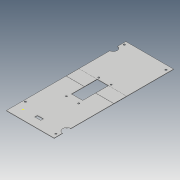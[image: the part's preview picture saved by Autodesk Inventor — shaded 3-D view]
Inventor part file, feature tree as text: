
AUTODESK INVENTOR PART (.ipt)
format: ipt  version: 2019 (Build 230136000, 136)  size: 241,152 bytes
history: native  units: mm
features: move_body x8, sketch x7, reference x6, extrude x5, other x5, direct_edit x3, plane x1, fillet x1, split x1
ambient origin geometry x8: Origin, YZ Plane, XZ Plane, XY Plane, X Axis, Y Axis, Z Axis, Center Point
bodies: Solid1 (feature_tree), Solid2 (feature_tree), Solid3 (feature_tree)
feature tree (37):
  plane  "Work Plane1"
  extrude  "Extrusion1"  Depth=2.0mm TaperAngle=0.0deg
  extrude  "Extrusion2"  Depth=29.0mm
  sketch  "Sketch3"  dims[d6=4.0mm d7=4.0mm d8=4.0mm]
  extrude  "Extrusion4"  Depth=4.0mm
  fillet  "Fillet1"  Radius=4.0mm
  extrude  "Extrusion5"  Depth=5.5mm
  split  "Split1"
  sketch  "Sketch7"  dims[d14=11.8mm d15=1.4mm d16=1.4mm d17=11.8mm d20=20.0mm d21=2.0mm d22=0.0mm d23=1.0mm d24=280.0mm d25=7.0mm d26=15.5mm d27=10.0mm d28=0.0mm d29=10.0mm d30=0.0mm d34=0.0mm d35=0.0mm d36=-1.0mm d37=0.0mm d38=0.0mm d39=-1.0mm d40=0.0mm d41=0.0mm d42=-1.0mm d43=0.0mm d44=0.0mm d45=-1.0mm d46=0.0mm d47=0.0mm d48=-1.0mm d49=0.0mm d50=0.0mm d51=-1.0mm d52=20.0mm d53=0.0mm d54=0.0mm d55=-1.0mm d56=0.0mm d57=0.0mm d58=-1.0mm d59=10.0mm d60=10.0mm d61=5.0mm]
  extrude  "Extrusion6"  Depth=1.4mm
  direct_edit  "Direct Edit1"
  direct_edit  "Direct Edit2"
  direct_edit  "Direct Edit3"
  sketch  "Sketch1"  dims[d0=2.0mm d1=0.0mm d2=2.0mm d3=0.0mm]
  reference  "Reference1"
  reference  "Reference2"
  sketch  "Sketch2"  dims[d4=66.5mm d5=29.0mm]
  reference  "Reference3"
  reference  "Reference4"
  reference  "Reference5"
  reference  "Reference6"
  sketch  "Sketch4"  dims[d9=4.0mm d10=5.5mm]
  sketch  "Sketch5"  dims[d11=5.5mm d12=1.4mm]
  sketch  "Sketch6"  dims[d13=1.4mm]
  parser-record x1  (decoder bookkeeping rows leaked as tree rows — omitted from the tree; the rows remain in map.json)
  other  "Placca B.iam"
  other  "Case_B1:1"
  other  "Case_B2:1"
  move_body  "Move2"
  move_body  "Move3"
  move_body  "Move4"
  move_body  "Move5"
  move_body  "Move6"
  move_body  "Move7"
  move_body  "Move8"
  move_body  "Move9"
  other  "Scale1"
note: 1 file-system path scrubbed to <path> (originals preserved in map.json)
